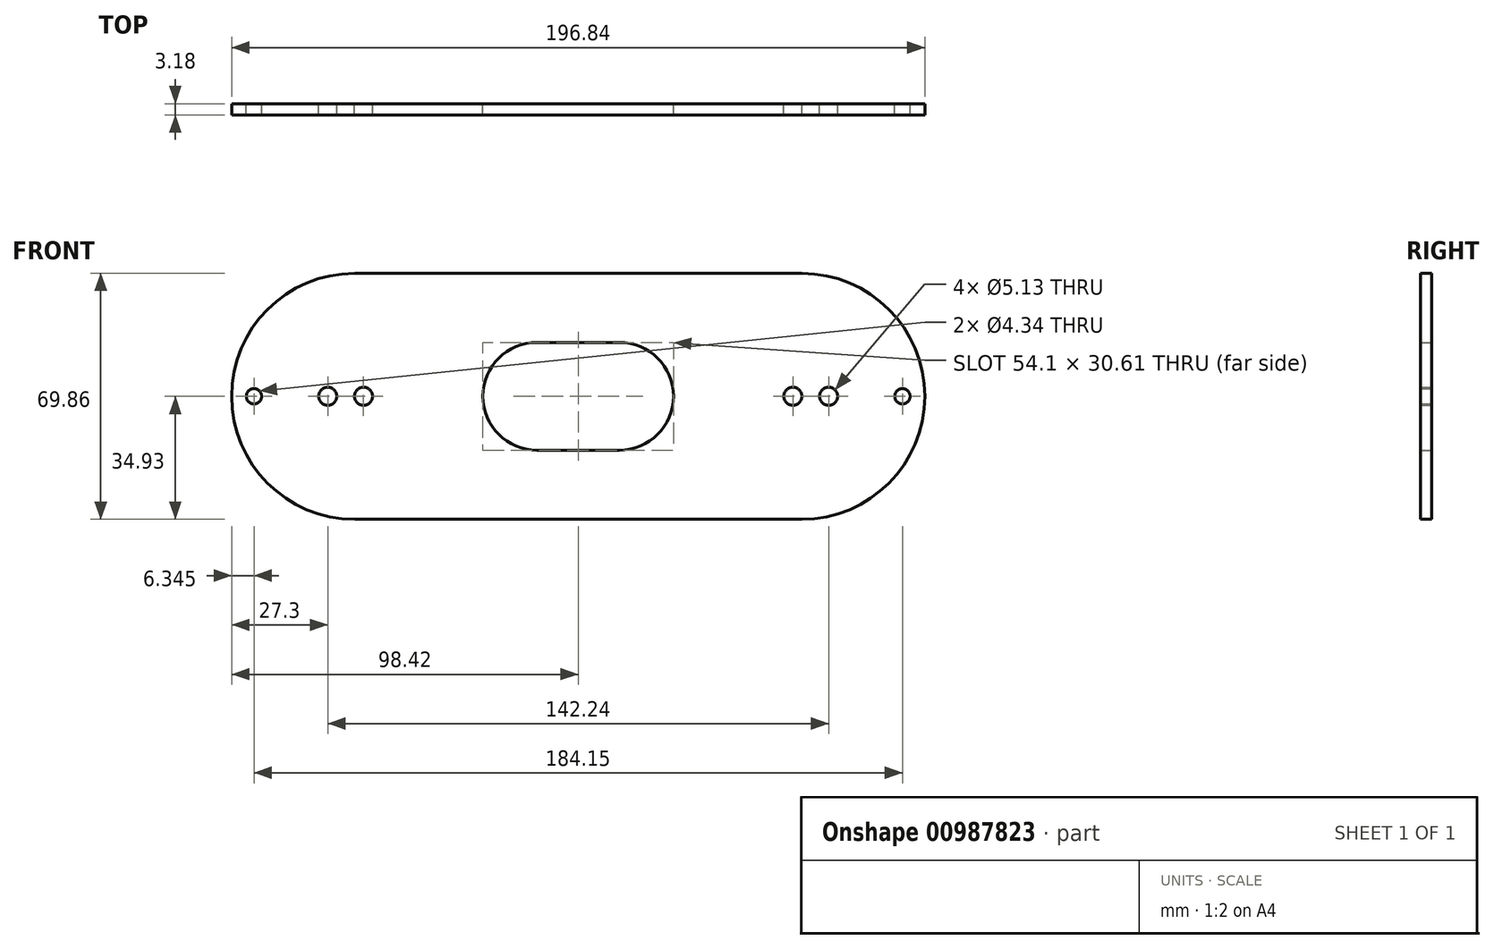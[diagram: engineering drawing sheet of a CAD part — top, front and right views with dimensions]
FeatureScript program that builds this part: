
annotation { "Feature Type Name" : "Feature", "Feature Type Description" : "" }
export const myFeature = defineFeature(function(context is Context, id is Id, definition is map)
    precondition{}
    {
        {
            var Q0;
            Q0=qCreatedBy(makeId("Front.planeOp"),FACE);
            var sketch = newSketch(context, id + "F0", { "sketchPlane" : qUnion([Q0])});
            skLineSegment(sketch, "E0.bottom", {"start": v(-63.5, 34.93) * mm, "end": v(63.5, 34.93) * mm});
            skLineSegment(sketch, "E0.top", {"start": v(-63.5, -34.92) * mm, "end": v(63.5, -34.93) * mm});
            skLineSegment(sketch, "E0.left", {"start": v(-98.43, 0) * mm, "end": v(-98.43, 0) * mm});
            skLineSegment(sketch, "E0.right", {"start": v(98.43, 0) * mm, "end": v(98.43, 0) * mm});
            skPoint(sketch, "E1.visualSharp", {"position": v(-98.43, 34.93) * mm});
            skArc(sketch, "E1.filletArc", {"start": v(-63.5, 34.92) * mm, "mid": v(-88.2, 24.7) * mm, "end": v(-98.43, 0) * mm});
            skPoint(sketch, "E2.visualSharp", {"position": v(-98.43, -34.92) * mm});
            skArc(sketch, "E2.filletArc", {"start": v(-98.43, 0) * mm, "mid": v(-88.2, -24.7) * mm, "end": v(-63.5, -34.92) * mm});
            skPoint(sketch, "E3.visualSharp", {"position": v(98.43, 34.92) * mm});
            skArc(sketch, "E3.filletArc", {"start": v(98.43, 0) * mm, "mid": v(88.2, 24.7) * mm, "end": v(63.5, 34.93) * mm});
            skPoint(sketch, "E4.visualSharp", {"position": v(98.43, -34.93) * mm});
            skArc(sketch, "E4.filletArc", {"start": v(63.5, -34.93) * mm, "mid": v(88.2, -24.7) * mm, "end": v(98.43, 0) * mm});
            skLineSegment(sketch, "E5.bottom", {"start": v(-11.75, 15.3) * mm, "end": v(11.75, 15.3) * mm});
            skLineSegment(sketch, "E5.top", {"start": v(-11.75, -15.3) * mm, "end": v(11.75, -15.3) * mm});
            skLineSegment(sketch, "E5.left", {"start": v(-27.05, 0) * mm, "end": v(-27.05, 0) * mm});
            skLineSegment(sketch, "E5.right", {"start": v(27.05, 0) * mm, "end": v(27.05, 0) * mm});
            skPoint(sketch, "E6.visualSharp", {"position": v(-27.05, 15.3) * mm});
            skArc(sketch, "E6.filletArc", {"start": v(-11.75, 15.3) * mm, "mid": v(-22.57, 10.82) * mm, "end": v(-27.05, 0) * mm});
            skPoint(sketch, "E7.visualSharp", {"position": v(-27.05, -15.3) * mm});
            skArc(sketch, "E7.filletArc", {"start": v(-27.05, 0) * mm, "mid": v(-22.57, -10.82) * mm, "end": v(-11.75, -15.3) * mm});
            skPoint(sketch, "E8.visualSharp", {"position": v(27.05, 15.3) * mm});
            skArc(sketch, "E8.filletArc", {"start": v(27.05, 0) * mm, "mid": v(22.57, 10.82) * mm, "end": v(11.75, 15.3) * mm});
            skPoint(sketch, "E9.visualSharp", {"position": v(27.05, -15.3) * mm});
            skArc(sketch, "E9.filletArc", {"start": v(11.75, -15.3) * mm, "mid": v(22.57, -10.82) * mm, "end": v(27.05, 0) * mm});
            skCircle(sketch, "E10", {"center": v(-92.08, 0) * mm, "radius": 2.17 * mm});
            skCircle(sketch, "E11", {"center": v(-71.12, 0) * mm, "radius": 2.57 * mm});
            skCircle(sketch, "E12", {"center": v(-60.96, 0) * mm, "radius": 2.57 * mm});
            skCircle(sketch, "E13", {"center": v(60.96, 0) * mm, "radius": 2.57 * mm});
            skCircle(sketch, "E14", {"center": v(71.12, 0) * mm, "radius": 2.57 * mm});
            skCircle(sketch, "E15", {"center": v(92.08, 0) * mm, "radius": 2.17 * mm});
            skSolve(sketch);
        }
        {
            var Q0;
            Q0=makeQuery(id+"F0.imprint","IMPRINT",FACE,{"disambiguationData":[TD([[makeQuery(id+"F0.imprint","IMPRINT",EDGE,{"derivedFrom":sQuery(id+"F0.wireOp",EDGE,"E0.bottom")}),-1.0]])]});
            extrude(context, id + "F1", {"entities" : qUnion([Q0]), "depth" : 3.17 * mm, "offsetDistance" : 25.4 * mm});
        }
    });
